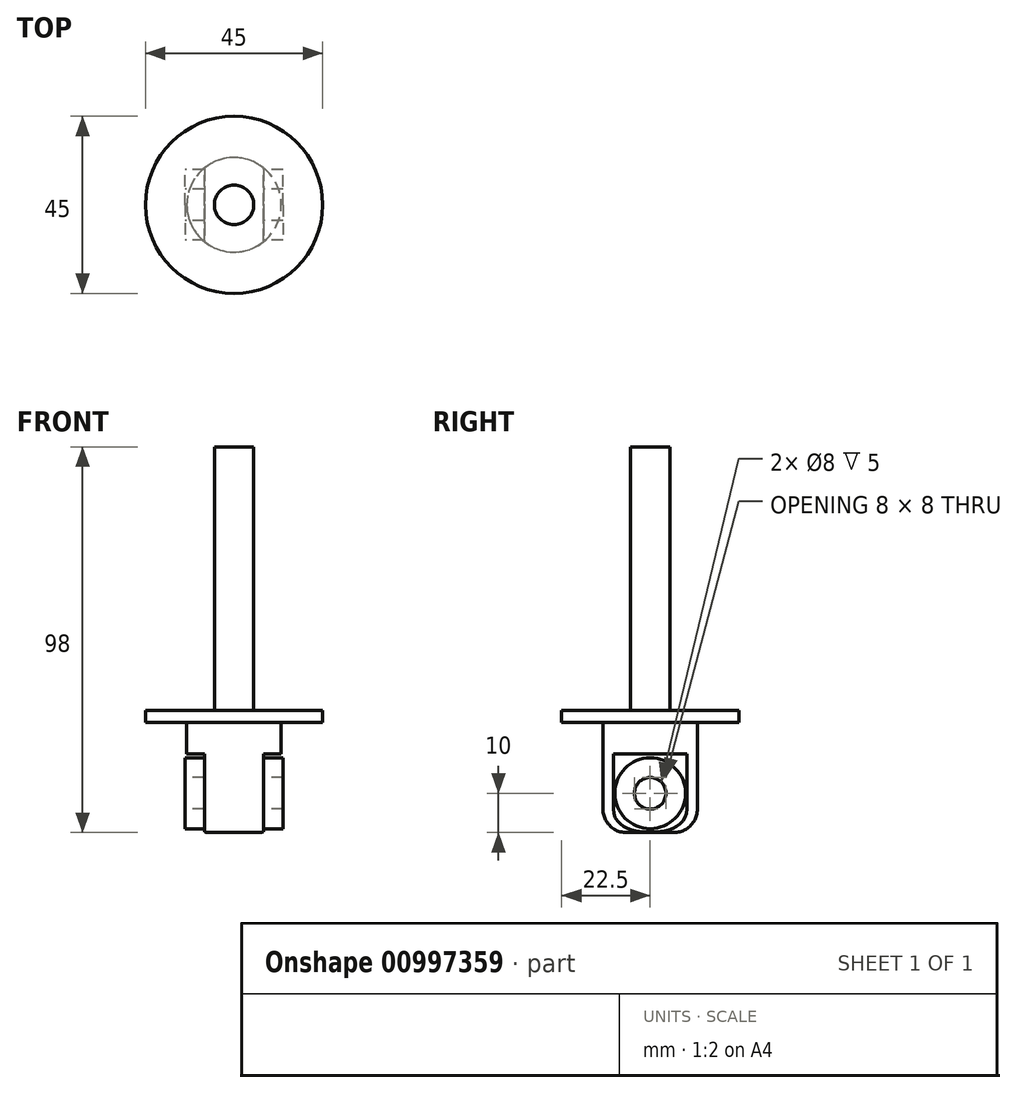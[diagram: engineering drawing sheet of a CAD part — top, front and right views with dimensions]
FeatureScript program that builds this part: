
annotation { "Feature Type Name" : "Feature", "Feature Type Description" : "" }
export const myFeature = defineFeature(function(context is Context, id is Id, definition is map)
    precondition{}
    {
        {
            var Q0;
            Q0=qCreatedBy(makeId("Top.planeOp"),FACE);
            var sketch = newSketch(context, id + "F0", { "sketchPlane" : qUnion([Q0])});
            skCircle(sketch, "E0", {"center": v(0, 0) * mm, "radius": 22.5 * mm});
            skSolve(sketch);
        }
        {
            var Q0;
            Q0 = qSketchRegion(id + "F0", true);
            extrude(context, id + "F1", {"entities" : qUnion([Q0]), "depth" : 3 * mm, "offsetDistance" : 25 * mm});
        }
        {
            var Q0;
            Q0=qCreatedBy(makeId("Top.planeOp"),FACE);
            var sketch = newSketch(context, id + "F2", { "sketchPlane" : qUnion([Q0])});
            skCircle(sketch, "E1", {"center": v(0, 0) * mm, "radius": 5 * mm});
            skSolve(sketch);
        }
        {
            var Q0;
            Q0 = qSketchRegion(id + "F2", true);
            extrude(context, id + "F3", {"entities" : qUnion([Q0]), "operationType" : NewBodyOperationType.ADD, "depth" : 70 * mm, "offsetDistance" : 25 * mm});
        }
        {
            var Q0;
            Q0=makeQuery(id+"F1.opExtrude","CAP_FACE",FACE,{"disambiguationData":[OSD([sQuery(id+"F0.wireOp",EDGE,"E0")])],"isStart":true});
            var sketch = newSketch(context, id + "F4", { "sketchPlane" : qUnion([Q0])});
            skCircle(sketch, "E2", {"center": v(0, 0) * mm, "radius": 12 * mm});
            skSolve(sketch);
        }
        {
            var Q0;
            Q0 = qSketchRegion(id + "F4", true);
            extrude(context, id + "F5", {"entities" : qUnion([Q0]), "operationType" : NewBodyOperationType.ADD, "depth" : 28 * mm, "offsetDistance" : 25 * mm});
        }
        {
            var Q0;
            Q0=makeQuery(id+"F5.opExtrude","CAP_EDGE",EDGE,{"disambiguationData":[OSD([sQuery(id+"F4.wireOp",EDGE,"E2")])],"isStart":false});
            fillet(context, id + "F6", {"entities" : qUnion([Q0]), "radius" : 6 * mm, "tangentPropagation" : true, "allowEdgeOverflow" : false});
        }
        {
            var Q0;
            Q0=qCreatedBy(makeId("Front.planeOp"),FACE);
            var sketch = newSketch(context, id + "F7", { "sketchPlane" : qUnion([Q0])});
            skLineSegment(sketch, "E3.bottom", {"start": v(7.5, -8) * mm, "end": v(27.07, -8) * mm});
            skLineSegment(sketch, "E3.top", {"start": v(7.5, -28) * mm, "end": v(27.07, -28) * mm});
            skLineSegment(sketch, "E3.left", {"start": v(7.5, -8) * mm, "end": v(7.5, -28) * mm});
            skLineSegment(sketch, "E3.right", {"start": v(27.07, -8) * mm, "end": v(27.07, -28) * mm});
            skLineSegment(sketch, "E4.MirrorCS", {"start": v(-27.07, -8) * mm, "end": v(-27.07, -28) * mm});
            skLineSegment(sketch, "E5.MirrorCS", {"start": v(-7.5, -8) * mm, "end": v(-7.5, -28) * mm});
            skLineSegment(sketch, "E6.MirrorCS", {"start": v(-7.5, -8) * mm, "end": v(-27.07, -8) * mm});
            skLineSegment(sketch, "E7.MirrorCS", {"start": v(-7.5, -28) * mm, "end": v(-27.07, -28) * mm});
            skSolve(sketch);
        }
        {
            var Q0;
            Q0=makeQuery(id+"F7.imprint","IMPRINT",FACE,{"disambiguationData":[TD([[makeQuery(id+"F7.imprint","IMPRINT",EDGE,{"derivedFrom":sQuery(id+"F7.wireOp",EDGE,"E3.bottom")}),-1.0]])]});
            var Q1;
            Q1=makeQuery(id+"F7.imprint","IMPRINT",FACE,{"disambiguationData":[TD([[makeQuery(id+"F7.imprint","IMPRINT",EDGE,{"derivedFrom":sQuery(id+"F7.wireOp",EDGE,"E4.MirrorCS")}),1.0]])]});
            extrude(context, id + "F8", {"entities" : qUnion([Q0, Q1]), "operationType" : NewBodyOperationType.REMOVE, "endBound" : BoundingType.SYMMETRIC, "oppositeDirection" : true, "depth" : 25 * mm, "offsetDistance" : 25 * mm});
        }
        {
            var Q0;
            Q0=qCreatedBy(makeId("Right.planeOp"),FACE);
            var sketch = newSketch(context, id + "F9", { "sketchPlane" : qUnion([Q0])});
            skCircle(sketch, "E8", {"center": v(0, -18) * mm, "radius": 4 * mm});
            skCircle(sketch, "E9", {"center": v(0, -18) * mm, "radius": 9 * mm});
            skSolve(sketch);
        }
        {
            var Q0;
            Q0 = qSketchRegion(id + "F9", true);
            extrude(context, id + "F10", {"entities" : qUnion([Q0]), "operationType" : NewBodyOperationType.ADD, "endBound" : BoundingType.SYMMETRIC, "depth" : 25 * mm, "offsetDistance" : 25 * mm});
        }
    });
